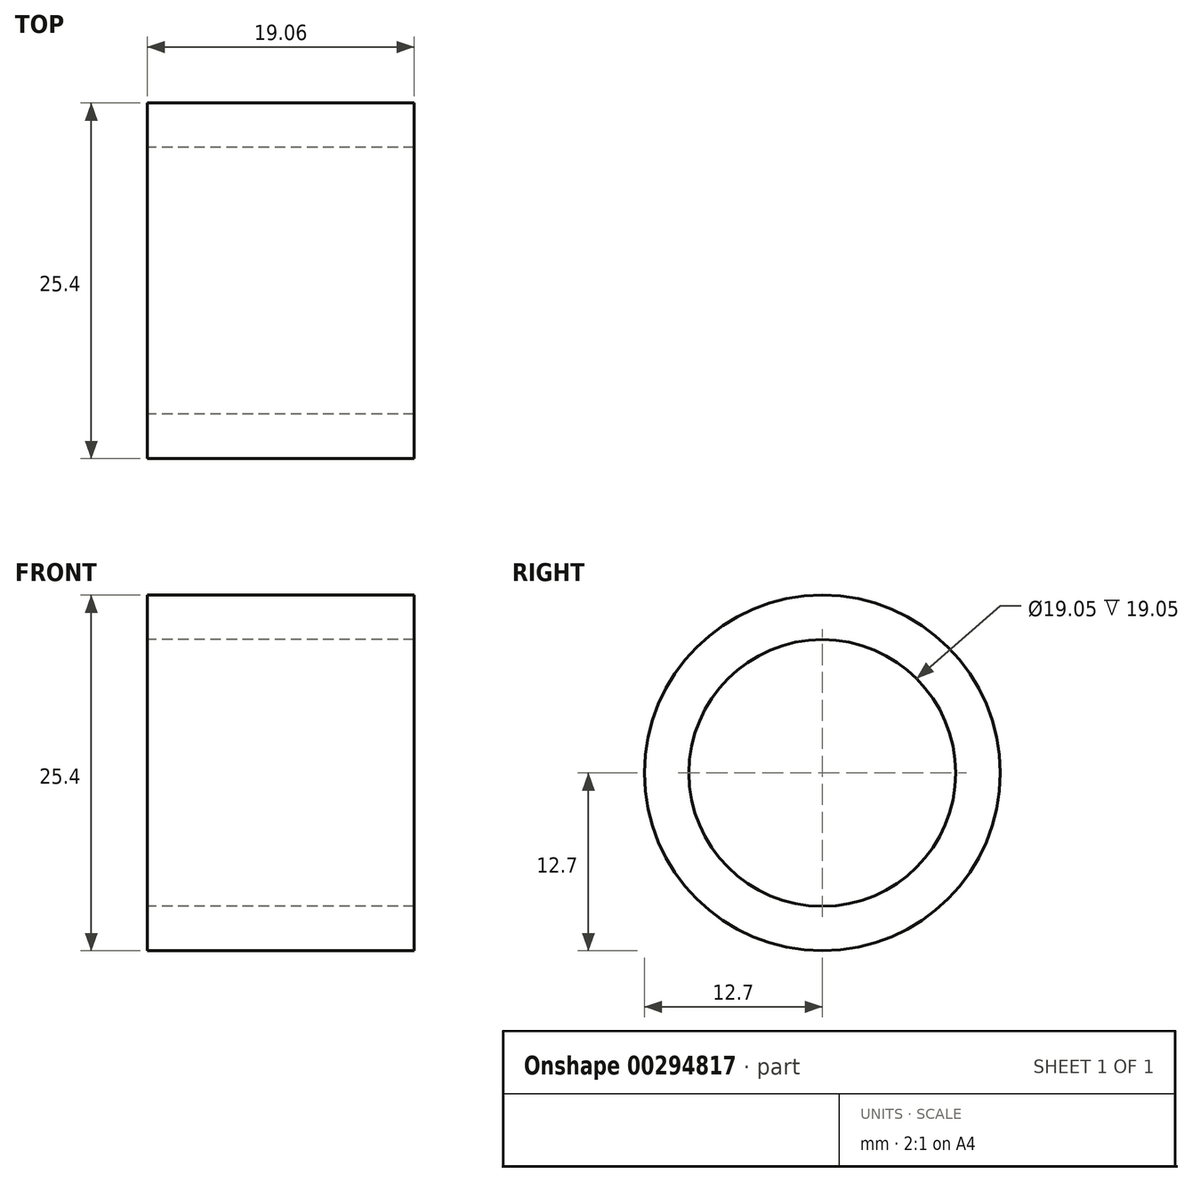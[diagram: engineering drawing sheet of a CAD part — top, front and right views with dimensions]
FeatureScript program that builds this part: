
annotation { "Feature Type Name" : "Feature", "Feature Type Description" : "" }
export const myFeature = defineFeature(function(context is Context, id is Id, definition is map)
    precondition{}
    {
        {
            var Q0;
            Q0=qCreatedBy(makeId("Right.planeOp"),FACE);
            var sketch = newSketch(context, id + "F0", { "sketchPlane" : qUnion([Q0])});
            skCircle(sketch, "E0", {"center": v(0, 0) * mm, "radius": 9.53 * mm});
            skCircle(sketch, "E1", {"center": v(0, 0) * mm, "radius": 12.7 * mm});
            skSolve(sketch);
        }
        {
            var Q0;
            Q0=makeQuery(id+"F0.imprint","IMPRINT",FACE,{"disambiguationData":[TD([[makeQuery(id+"F0.imprint","IMPRINT",EDGE,{"derivedFrom":sQuery(id+"F0.wireOp",EDGE,"E0")}),-1.0]])]});
            extrude(context, id + "F1", {"entities" : qUnion([Q0]), "endBound" : BoundingType.SYMMETRIC, "depth" : 19.05 * mm});
        }
    });
